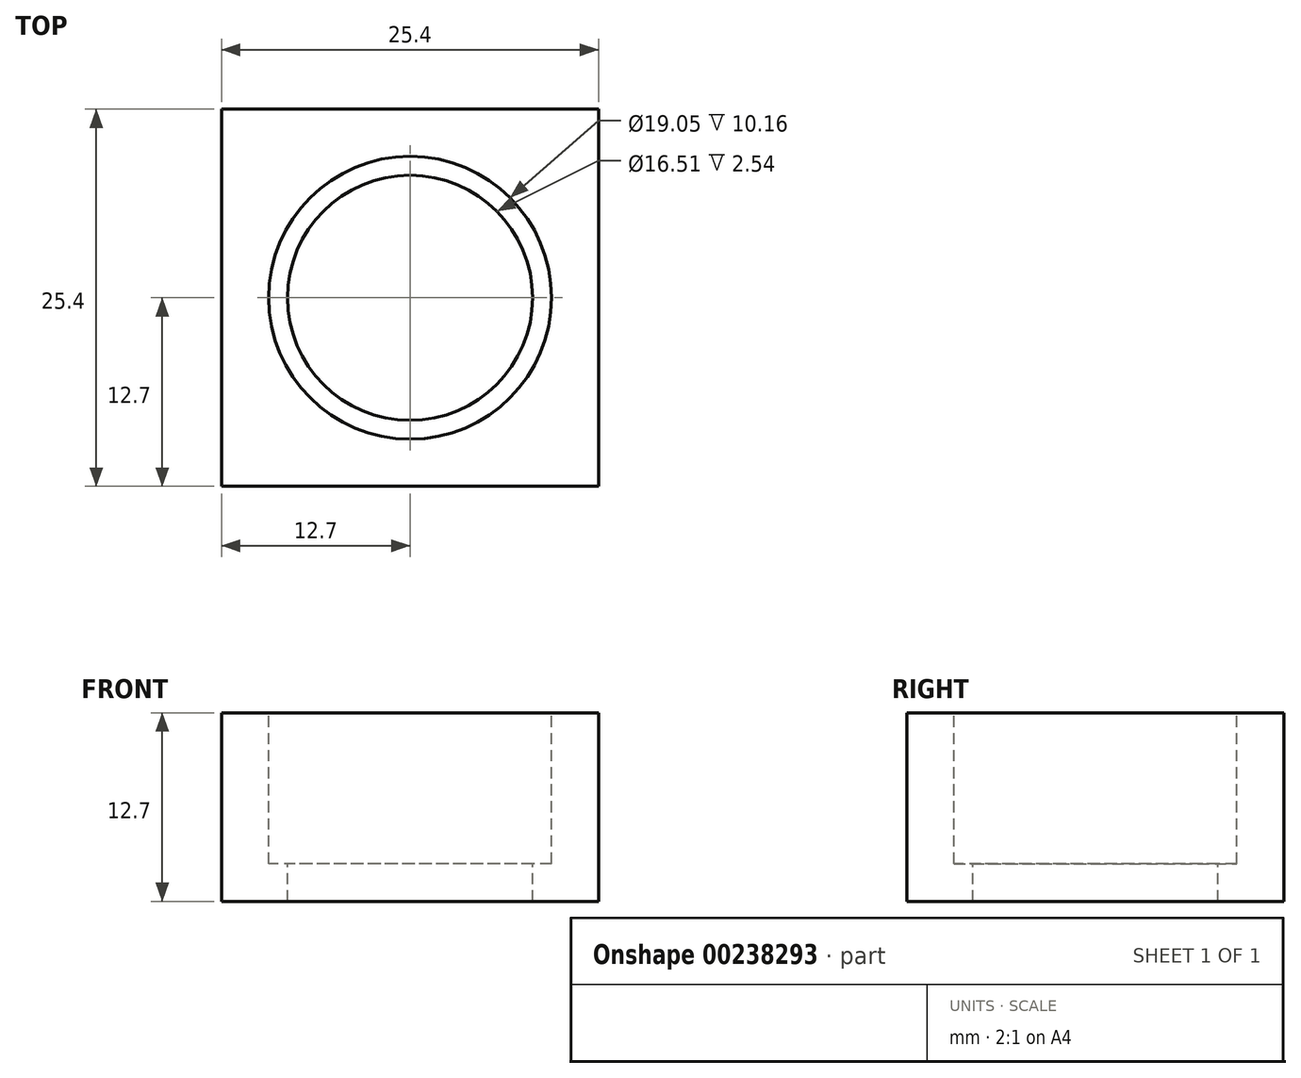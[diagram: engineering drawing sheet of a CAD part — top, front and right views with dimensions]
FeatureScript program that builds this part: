
annotation { "Feature Type Name" : "Feature", "Feature Type Description" : "" }
export const myFeature = defineFeature(function(context is Context, id is Id, definition is map)
    precondition{}
    {
        {
            var Q0;
            Q0=qCreatedBy(makeId("Top.planeOp"),FACE);
            var sketch = newSketch(context, id + "F0", { "sketchPlane" : qUnion([Q0])});
            skLineSegment(sketch, "E0.bottom", {"start": v(0, 0) * mm, "end": v(25.4, 0) * mm});
            skLineSegment(sketch, "E0.top", {"start": v(0, 25.4) * mm, "end": v(25.4, 25.4) * mm});
            skLineSegment(sketch, "E0.left", {"start": v(0, 0) * mm, "end": v(0, 25.4) * mm});
            skLineSegment(sketch, "E0.right", {"start": v(25.4, 0) * mm, "end": v(25.4, 25.4) * mm});
            skSolve(sketch);
        }
        {
            var Q0;
            Q0=makeQuery(id+"F0.imprint","IMPRINT",FACE,{"disambiguationData":[TD([[makeQuery(id+"F0.imprint","IMPRINT",EDGE,{"derivedFrom":sQuery(id+"F0.wireOp",EDGE,"E0.bottom")}),1.0]])]});
            extrude(context, id + "F1", {"entities" : qUnion([Q0]), "depth" : 12.7 * mm});
        }
        {
            var Q0;
            Q0=makeQuery(id+"F1.opExtrude","CAP_FACE",FACE,{"disambiguationData":[OSD([sQuery(id+"F0.wireOp",EDGE,"E0.bottom"),sQuery(id+"F0.wireOp",EDGE,"E0.top"),sQuery(id+"F0.wireOp",EDGE,"E0.left"),sQuery(id+"F0.wireOp",EDGE,"E0.right")])],"isStart":false});
            var sketch = newSketch(context, id + "F2", { "sketchPlane" : qUnion([Q0])});
            skCircle(sketch, "E1", {"center": v(12.7, 12.7) * mm, "radius": 9.53 * mm});
            skPoint(sketch, "E1.centerSnap0", {"position": v(25.4, 12.7) * mm});
            skPoint(sketch, "E1.centerSnap1", {"position": v(12.7, 25.4) * mm});
            skSolve(sketch);
        }
        {
            var Q0;
            Q0 = qSketchRegion(id + "F2", true);
            extrude(context, id + "F3", {"entities" : qUnion([Q0]), "operationType" : NewBodyOperationType.REMOVE, "oppositeDirection" : true, "depth" : 10.16 * mm});
        }
        {
            var Q0;
            Q0=makeQuery(id+"F3.boolean.opBoolean","COPY",FACE,{"derivedFrom":makeQuery(id+"F3.opExtrude","CAP_FACE",FACE,{"disambiguationData":[OSD([sQuery(id+"F2.wireOp",EDGE,"E1")])],"isStart":false})});
            var sketch = newSketch(context, id + "F4", { "sketchPlane" : qUnion([Q0])});
            skCircle(sketch, "E2", {"center": v(12.7, 12.7) * mm, "radius": 8.26 * mm});
            skSolve(sketch);
        }
        {
            var Q0;
            Q0 = qSketchRegion(id + "F4", true);
            extrude(context, id + "F5", {"entities" : qUnion([Q0]), "operationType" : NewBodyOperationType.REMOVE, "endBound" : BoundingType.THROUGH_ALL, "oppositeDirection" : true, "depth" : 25.4 * mm});
        }
    });
